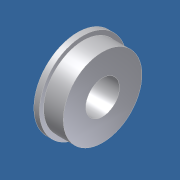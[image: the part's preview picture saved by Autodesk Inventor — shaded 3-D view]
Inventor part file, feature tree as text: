
AUTODESK INVENTOR PART (.ipt)
format: ipt  version: unknown  size: 186,368 bytes
history: native  units: in
note: dims shown in document units (in); Inventor stores cm internally (conversion verified against a paired STEP export)
features: revolve x1, imported_body x1
ambient origin geometry x8: Origin, YZ Plane, XZ Plane, XY Plane, X Axis, Y Axis, Z Axis, Center Point
feature tree (2):
  revolve  "Revolve1"  [1 undecoded]
  imported_body  "Base1"
note: 1 required parameter value undecoded (feature->parameter linkage not recoverable at this tier; creation-order binding heuristic only, values carry confidence <= 0.55)
